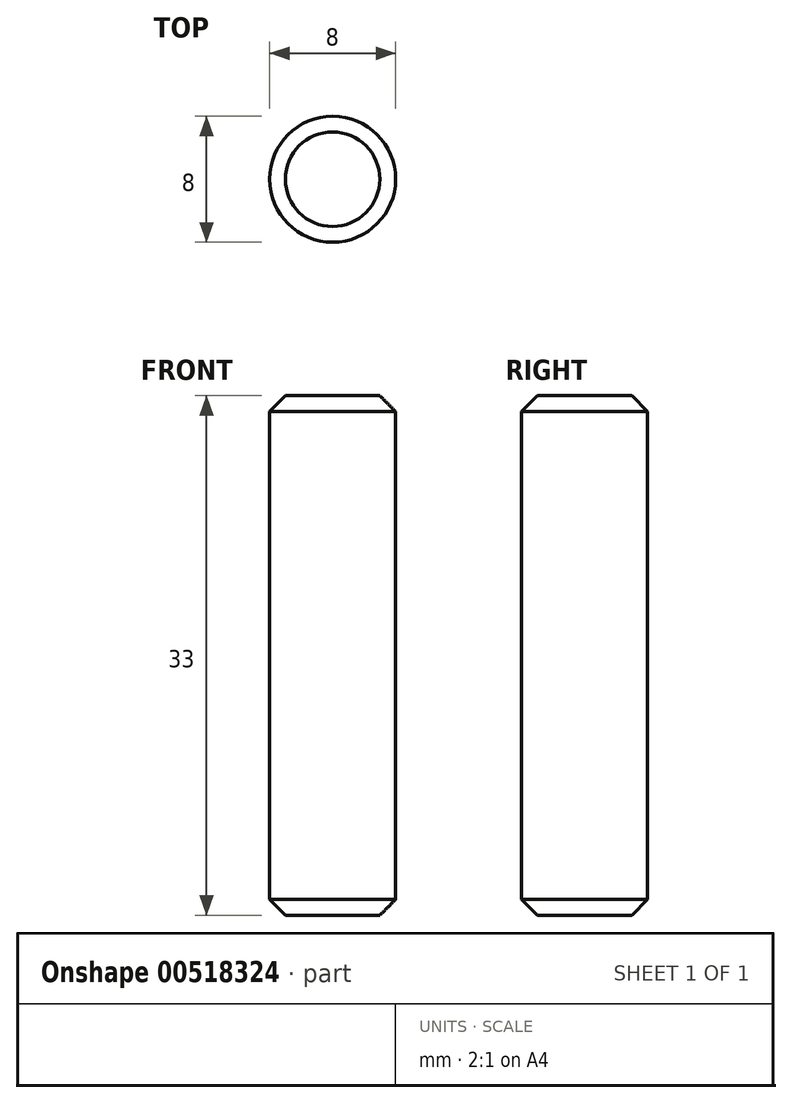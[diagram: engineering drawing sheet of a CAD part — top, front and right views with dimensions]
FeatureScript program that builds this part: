
annotation { "Feature Type Name" : "Feature", "Feature Type Description" : "" }
export const myFeature = defineFeature(function(context is Context, id is Id, definition is map)
    precondition{}
    {
        {
            var Q0;
            Q0=qCreatedBy(makeId("Top.planeOp"),FACE);
            var sketch = newSketch(context, id + "F0", { "sketchPlane" : qUnion([Q0])});
            skCircle(sketch, "E0", {"center": v(0, 0) * mm, "radius": 4 * mm});
            skSolve(sketch);
        }
        {
            var Q0;
            Q0=makeQuery(id+"F0.imprint","IMPRINT",FACE,{"disambiguationData":[TD([[makeQuery(id+"F0.imprint","IMPRINT",EDGE,{"derivedFrom":sQuery(id+"F0.wireOp",EDGE,"E0")}),1.0]])]});
            extrude(context, id + "F1", {"entities" : qUnion([Q0]), "depth" : 33 * mm, "offsetDistance" : 25 * mm});
        }
        {
            var Q0;
            Q0=makeQuery(id+"F1.opExtrude","CAP_EDGE",EDGE,{"disambiguationData":[OSD([sQuery(id+"F0.wireOp",EDGE,"E0")])],"isStart":false});
            var Q1;
            Q1=makeQuery(id+"F1.opExtrude","CAP_EDGE",EDGE,{"disambiguationData":[OSD([sQuery(id+"F0.wireOp",EDGE,"E0")])],"isStart":true});
            chamfer(context, id + "F2", {"entities" : qUnion([Q0, Q1]), "width" : 1 * mm, "tangentPropagation" : true});
        }
    });
